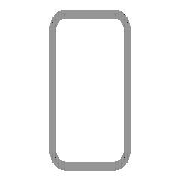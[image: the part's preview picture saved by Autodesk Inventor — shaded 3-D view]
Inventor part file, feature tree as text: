
AUTODESK INVENTOR PART (.ipt)
format: ipt  version: 2025 (Build 290162010, 162A)  size: 146,432 bytes
history: native  units: mm (DEFAULTED — no unit token found)
features: other x3, sketch x2, extrude x1, plane x1
ambient origin geometry x8: Origin, YZ Plane, XZ Plane, XY Plane, X Axis, Y Axis, Z Axis, Center Point
bodies: Solid1 (feature_tree), Body (feature_tree)
feature tree (7):
  other  "Driven Length"
  other  "Start plane"
  other  "End plane"
  extrude  "Extrusion2"  TaperAngle=0.0deg  [1 undecoded]
  sketch  "Sketch3"  dims[d3=200.0mm d4=0.0mm]
  plane  "Work Plane3"
  sketch  "Sketch5"  dims[d7=4.0mm d9=20.0mm d11=40.0mm d12=2.0mm d13=-0.0mm d14=200.0mm d15=10.0mm d16=20.0mm d17=90.0deg d18=200.0mm d19=0.0mm d20=0.0mm d22=40.0mm d23=45.0deg]
note: 1 required parameter value undecoded (feature->parameter linkage not recoverable at this tier; creation-order binding heuristic only, values carry confidence <= 0.55)
